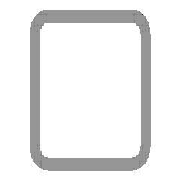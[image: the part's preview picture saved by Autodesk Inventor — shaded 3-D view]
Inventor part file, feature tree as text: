
AUTODESK INVENTOR PART (.ipt)
format: ipt  version: 2025.1 (Build 291241020, 241B)  size: 133,632 bytes
history: native  units: mm (DEFAULTED — no unit token found)
features: other x4, sketch x1, plane x1
ambient origin geometry x8: Origin, YZ Plane, XZ Plane, XY Plane, X Axis, Y Axis, Z Axis, Center Point
bodies: Solid1 (feature_tree), Body (feature_tree)
feature tree (6):
  parser-record x1  (decoder bookkeeping rows leaked as tree rows — omitted from the tree; the rows remain in map.json)
  other  "Driven Length"
  other  "Start Plane"
  other  "End Plane"
  sketch  "Sketch3"  dims[d3=550.0mm d4=0.0mm d7=4.0mm d9=40.0mm d11=40.0mm d12=2.0mm d13=100.0mm d14=650.0mm d15=20.0mm d16=20.0mm d17=90.0deg d18=550.0mm]
  plane  "Work Plane3"
